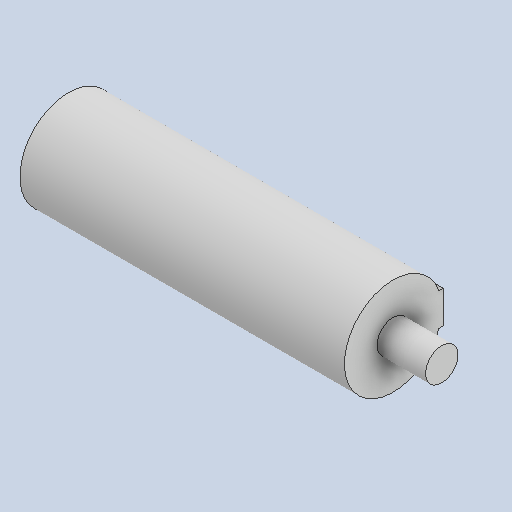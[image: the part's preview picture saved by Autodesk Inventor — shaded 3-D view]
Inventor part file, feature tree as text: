
AUTODESK INVENTOR PART (.ipt)
format: ipt  version: 2023 (Build 270158000, 158)  size: 115,712 bytes
history: native  units: mm
features: extrude x3, sketch x3, projected_geometry x1
ambient origin geometry x8: Origin, YZ Plane, XZ Plane, XY Plane, X Axis, Y Axis, Z Axis, Center Point
bodies: Solid1 (feature_tree)
feature tree (7):
  extrude  "Extrusion1"  Depth=20.0mm TaperAngle=0.0deg
  extrude  "Extrusion2"  Depth=3.0mm TaperAngle=0.0deg
  extrude  "Extrusion3"  Depth=2.0mm
  sketch  "Sketch1"  dims[d0=6.0mm d1=20.0mm d2=0.0mm]
  sketch  "Sketch2"  dims[d3=2.0mm d4=3.0mm d5=0.0mm]
  sketch  "Sketch3"  dims[d6=0.1mm d7=2.0mm d8=10.0mm d9=0.0mm]
  projected_geometry  "Projected Loop1"
